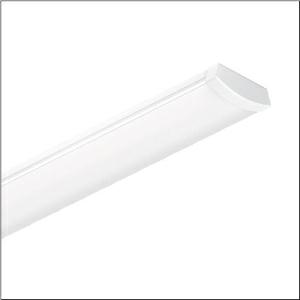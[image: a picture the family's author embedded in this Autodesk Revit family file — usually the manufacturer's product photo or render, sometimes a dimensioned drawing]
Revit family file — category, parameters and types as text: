
# Revit family: siluette_r__21_51ln12mnm70a3g_252a
name_source: partatom
category: Lighting Fixtures
units: mm (PartAtom-declared; Revit-internal decimal feet)

## family parameters
Cut with Voids When Loaded = No
Host = Face
Light Source = No
Part Type = Normal
Room Calculation Point = No
Round Connector Dimension = Use Diameter
Shared = No

## types (1)
- --- (1 x LED, 4320 lm, 28.8 W, 5000K)
    Apparent Load = 29 VA
    CIE Flux Codes = 43 73 92 94 100
    Color Rendering = 80
    Color Temperature = 5000K
    Default Elevation = 1800 mm
    Description = Siluette® 21, office luminaire, primary optical cover: enclosure, of PC, frosted, light emission: direct distribution, primary light characteristic: symmetric, installation type: suspended mounting, surface-mounted, LED, rated luminous flux: 7.150lm, luminous efficacy: 140lm/W, light colour: 830/840/850, colour temperature: 3000/4000/5000K, with terminal, 4-pole, mains connection: 220..240V, AC, 50/60Hz, rated input power: 50W, control gear: single battery element, housing, of sheet steel, white, length: 1.500mm, width: 152mm, height: 53mm, end cap, of PMMA, white, protection rating (complete): IP44, insulation class (complete): insulation class I (protective earthing), certification: CE, UKCA, protection symbol: D, permissible operating ambient temperature: -20..+40°C, standard: EN 60598-2-22, corresponds to IFS (International Featured Standards) requirements for safety and quality in the food industry, contact your sales advisor before using the luminaires in applications with unclear chemical exposure, large temperature fluctuations or condensation-forming humidity, packaging unit: 1 piece
    Height = 52 mm  [stored 0.170604 ft]
    Lamp = 1 x LED
    Lamp Light Flux = 4320 lm
    Lamp Power = 28.8 W
    Lamp count = 1
    Length = 1485 mm
    Luminous efficacy = 150 lm/W
    Manufacturer = Siteco
    ModVariant = No
    Model = 51LN12MNM70A3G
    Mounting Place = Ceiling
    Mounting Type = Pendant
    Number of Poles = 1
    OnlyDefault = Yes
    Power Factor = 1
    Product Name = Siluette® 21
    Product group = office luminaire | ceiling pendant
    ProductGroupID = 902
    Protection Class = Protection class I
    Protection Degree = IP 44
    RLX_Detail_Level = 1
    RLX_Emergency_Light_Flux = 0 lm
    RLX_Emergency_Type = 0
    RLX_Emergency_Type_DB = No
    RlxData = <blob elided: 20525 chars, md5=7809f61c>
    Socket = socket
    Standby Power = 0 W
    System Light Flux = 4320 lm
    System Power = 29 W
    Type Comments = individual setting: colour temperature 5000K, luminous flux: 61 % | (OFF | OFF | ON) | 200 mA
    Type Image = l_1296910.jpg
    URL = http://relux.com
    VarID = @adj_019167
    Voltage = 0 V
    Weight = 0.00 kg
    Width = 152 mm

note: [stored X ft] marks values corroborated as IEEE doubles in the binary element streams (Revit-internal decimal feet)

## geometry (parser evidence)
native form markers: Blend x4, Sweep x12
no freeform markers — native parametric forms only
